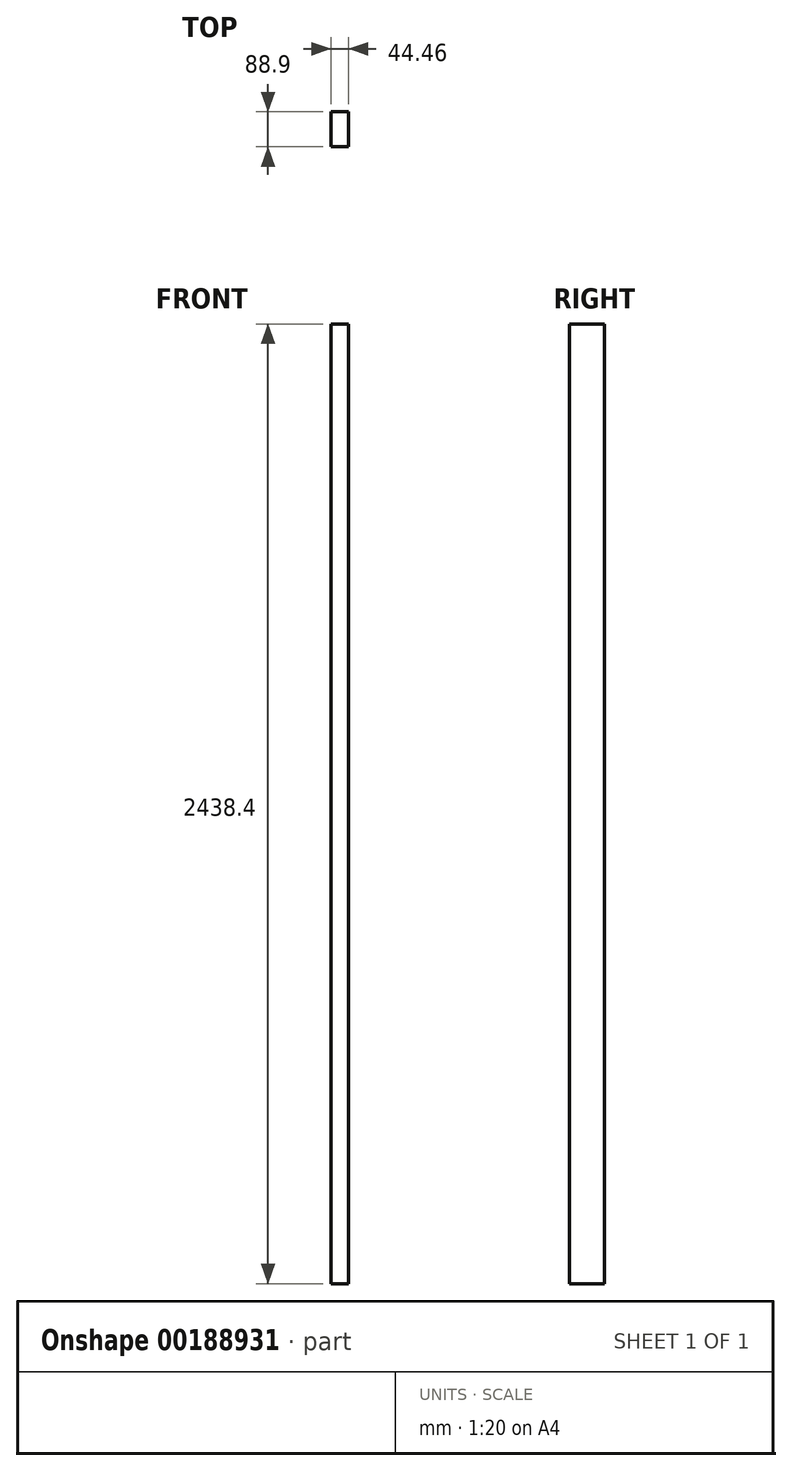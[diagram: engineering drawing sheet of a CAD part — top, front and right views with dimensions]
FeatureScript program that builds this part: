
annotation { "Feature Type Name" : "Feature", "Feature Type Description" : "" }
export const myFeature = defineFeature(function(context is Context, id is Id, definition is map)
    precondition{}
    {
        {
            var Q0;
            Q0=qCreatedBy(makeId("Top.planeOp"),FACE);
            var sketch = newSketch(context, id + "F1", { "sketchPlane" : qUnion([Q0])});
            skLineSegment(sketch, "E0.bottom", {"start": v(22.23, -44.45) * mm, "end": v(-22.22, -44.45) * mm});
            skLineSegment(sketch, "E0.top", {"start": v(22.22, 44.45) * mm, "end": v(-22.23, 44.45) * mm});
            skLineSegment(sketch, "E0.left", {"start": v(22.23, -44.45) * mm, "end": v(22.22, 44.45) * mm});
            skLineSegment(sketch, "E0.right", {"start": v(-22.22, -44.45) * mm, "end": v(-22.23, 44.45) * mm});
            skPoint(sketch, "E0.middle", {"position": v(0, 0) * mm});
            skSolve(sketch);
        }
        {
            var Q0;
            Q0=makeQuery(id+"F1.imprint","IMPRINT",FACE,{"disambiguationData":[TD([[makeQuery(id+"F1.imprint","IMPRINT",EDGE,{"derivedFrom":sQuery(id+"F1.wireOp",EDGE,"E0.bottom")}),-1.0]])]});
            extrude(context, id + "F0", {"entities" : qUnion([Q0]), "endBound" : BoundingType.SYMMETRIC, "depth" : 2438.4 * mm});
        }
    });
